AUTODESK INVENTOR PART (.ipt)
format: ipt  version: 2017 (Build 210142000, 142)  size: 202,752 bytes
history: native  units: mm
features: extrude x3, sketch x2, revolve x1, pattern_circular x1
ambient origin geometry x8: Origin, YZ Plane, XZ Plane, XY Plane, X Axis, Y Axis, Z Axis, Center Point
bodies: Solid1 (feature_tree)
feature tree (7):
  revolve  "Revolution1"  Angle=45.0deg
  extrude  "Extrusion1"  TaperAngle=360.0deg  [1 undecoded]
  pattern_circular  "Circular Pattern1"  [2 undecoded]
  extrude  "Extrusion2"  Depth=98.0mm
  extrude  "Extrusion3"  Depth=47.0mm
  sketch  "Sketch2"  dims[d10=90.0deg d13=45.0deg]
  sketch  "Sketch4"  dims[d14=10.0mm d15=0.0mm d17=360.0deg d29=26.0mm d30=98.0mm d31=47.0mm d32=127.5mm d33=24.0mm d34=39.0mm d35=20.0mm d37=50.0mm d38=0.0mm d39=15.5mm d40=10.0mm d41=0.0mm d42=0.0mm d43=0.0mm]
note: 3 required parameter values undecoded (feature->parameter linkage not recoverable at this tier; creation-order binding heuristic only, values carry confidence <= 0.55)
